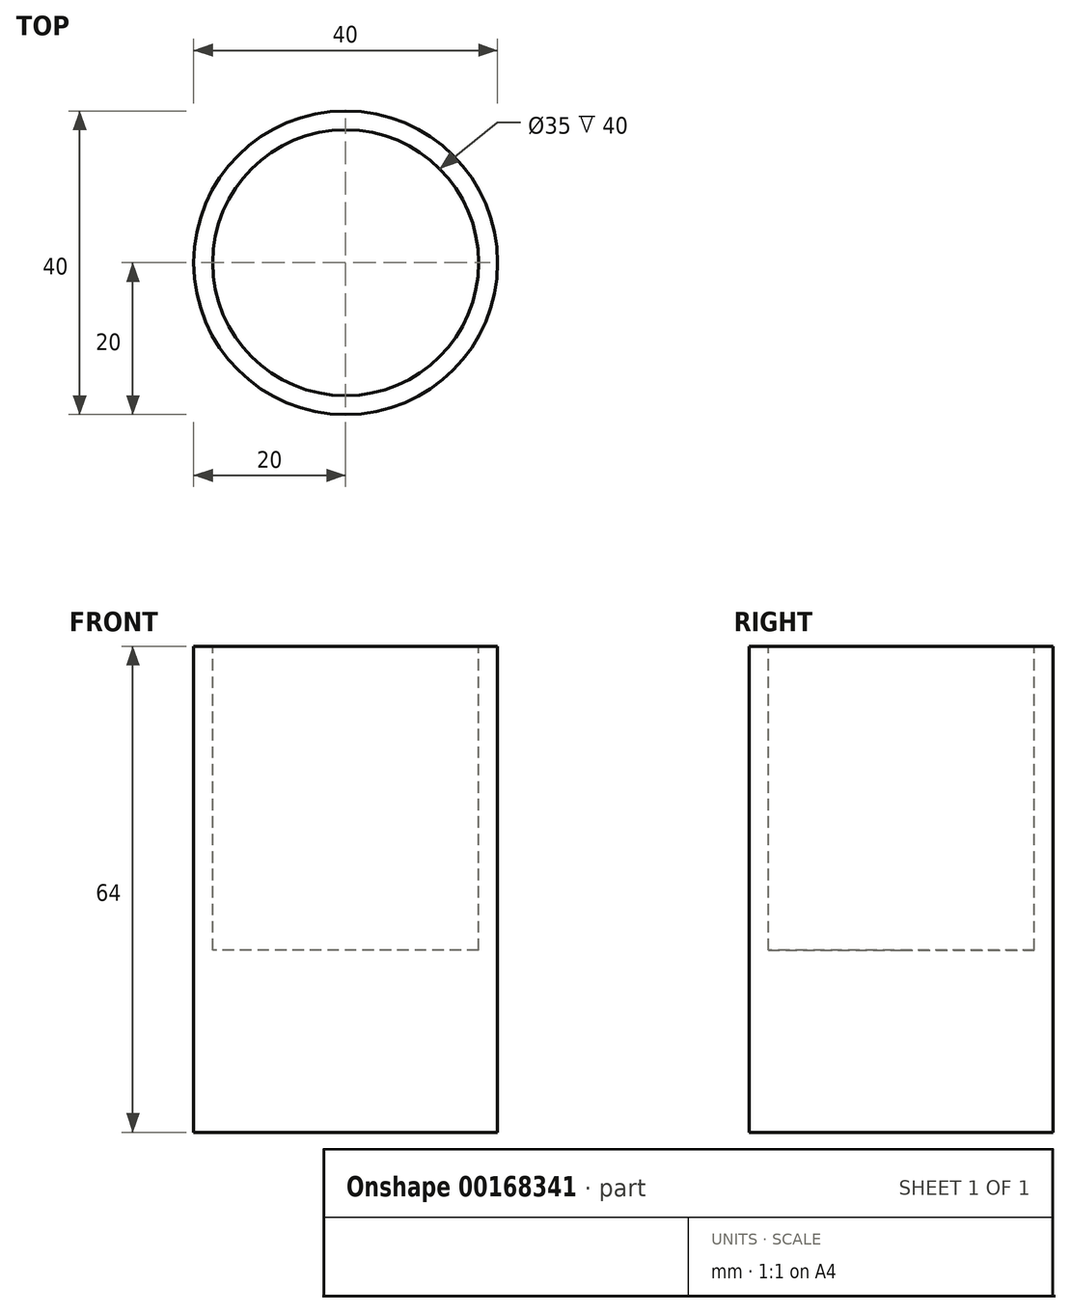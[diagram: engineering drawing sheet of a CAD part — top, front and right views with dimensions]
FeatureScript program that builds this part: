
annotation { "Feature Type Name" : "Feature", "Feature Type Description" : "" }
export const myFeature = defineFeature(function(context is Context, id is Id, definition is map)
    precondition{}
    {
        {
            var Q0;
            Q0=qCreatedBy(makeId("Top.planeOp"),FACE);
            var sketch = newSketch(context, id + "F0", { "sketchPlane" : qUnion([Q0])});
            skCircle(sketch, "E0", {"center": v(0, 0) * mm, "radius": 20 * mm});
            skSolve(sketch);
        }
        {
            var Q0;
            Q0=makeQuery(id+"F0.imprint","IMPRINT",FACE,{"disambiguationData":[TD([[makeQuery(id+"F0.imprint","IMPRINT",EDGE,{"derivedFrom":sQuery(id+"F0.wireOp",EDGE,"E0")}),1.0]])]});
            extrude(context, id + "F1", {"entities" : qUnion([Q0]), "oppositeDirection" : true, "depth" : 64 * mm});
        }
        {
            var Q0;
            Q0=makeQuery(id+"F1.opExtrude","CAP_FACE",FACE,{"disambiguationData":[OSD([sQuery(id+"F0.wireOp",EDGE,"E0")])],"isStart":true});
            var sketch = newSketch(context, id + "F2", { "sketchPlane" : qUnion([Q0])});
            skCircle(sketch, "E1", {"center": v(0, 0) * mm, "radius": 17.5 * mm});
            skSolve(sketch);
        }
        {
            var Q0;
            Q0=makeQuery(id+"F2.imprint","IMPRINT",FACE,{"disambiguationData":[TD([[makeQuery(id+"F2.imprint","IMPRINT",EDGE,{"derivedFrom":sQuery(id+"F2.wireOp",EDGE,"E1")}),1.0]])]});
            extrude(context, id + "F3", {"entities" : qUnion([Q0]), "operationType" : NewBodyOperationType.REMOVE, "oppositeDirection" : true, "depth" : 40 * mm});
        }
    });
